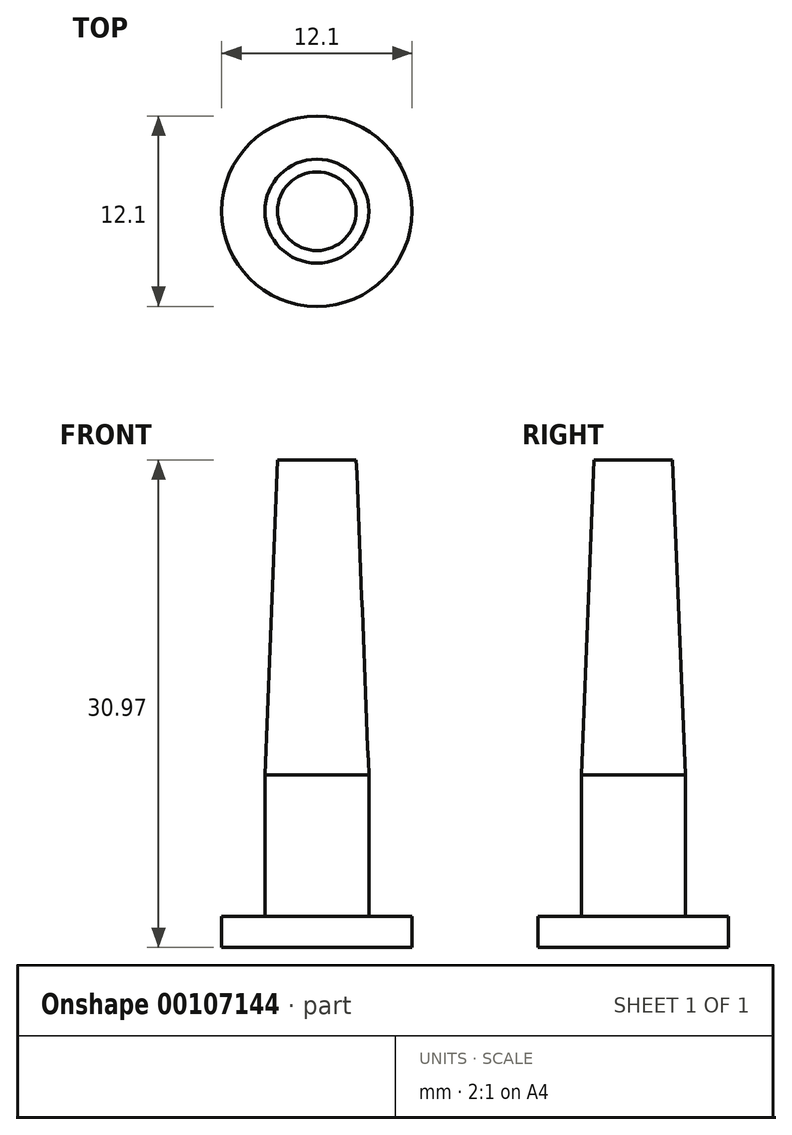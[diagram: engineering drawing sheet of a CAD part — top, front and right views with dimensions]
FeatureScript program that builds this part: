
annotation { "Feature Type Name" : "Feature", "Feature Type Description" : "" }
export const myFeature = defineFeature(function(context is Context, id is Id, definition is map)
    precondition{}
    {
        {
            var Q0;
            Q0=qCreatedBy(makeId("Front.planeOp"),FACE);
            var sketch = newSketch(context, id + "F0", { "sketchPlane" : qUnion([Q0])});
            skLineSegment(sketch, "E0", {"start": v(0, 20) * mm, "end": v(0, -21.45) * mm, "construction": true});
            skLineSegment(sketch, "E1", {"start": v(0, -21.45) * mm, "end": v(-0.64, -21.45) * mm, "construction": true});
            skLineSegment(sketch, "E2", {"start": v(-3.3, -8.97) * mm, "end": v(-3.3, 0) * mm});
            skLineSegment(sketch, "E3", {"start": v(-3.3, 0) * mm, "end": v(-2.5, 20) * mm});
            skLineSegment(sketch, "E4", {"start": v(-2.5, 20) * mm, "end": v(0, 20) * mm});
            skLineSegment(sketch, "E5", {"start": v(0, 20) * mm, "end": v(0, -10) * mm});
            skLineSegment(sketch, "E6.bottom", {"start": v(-6.05, -8.97) * mm, "end": v(-3.3, -8.97) * mm});
            skLineSegment(sketch, "E6.top", {"start": v(-6.05, -10.97) * mm, "end": v(0, -10.97) * mm});
            skLineSegment(sketch, "E6.left", {"start": v(-6.05, -8.97) * mm, "end": v(-6.05, -10.97) * mm});
            skLineSegment(sketch, "E6.right", {"start": v(0, -8.97) * mm, "end": v(0, -10.97) * mm});
            skPoint(sketch, "E7.end.orphan", {"position": v(-3.3, -10) * mm});
            skSolve(sketch);
        }
        {
            var Q0;
            Q0 = qSketchRegion(id + "F0", true);
            var Q1;
            Q1=sQuery(id+"F0.wireOp",EDGE,"E5");
            revolve(context, id + "F1", {"entities" : qUnion([Q0]), "axis" : qUnion([Q1]), "revolveType" : RevolveType.FULL});
        }
    });
